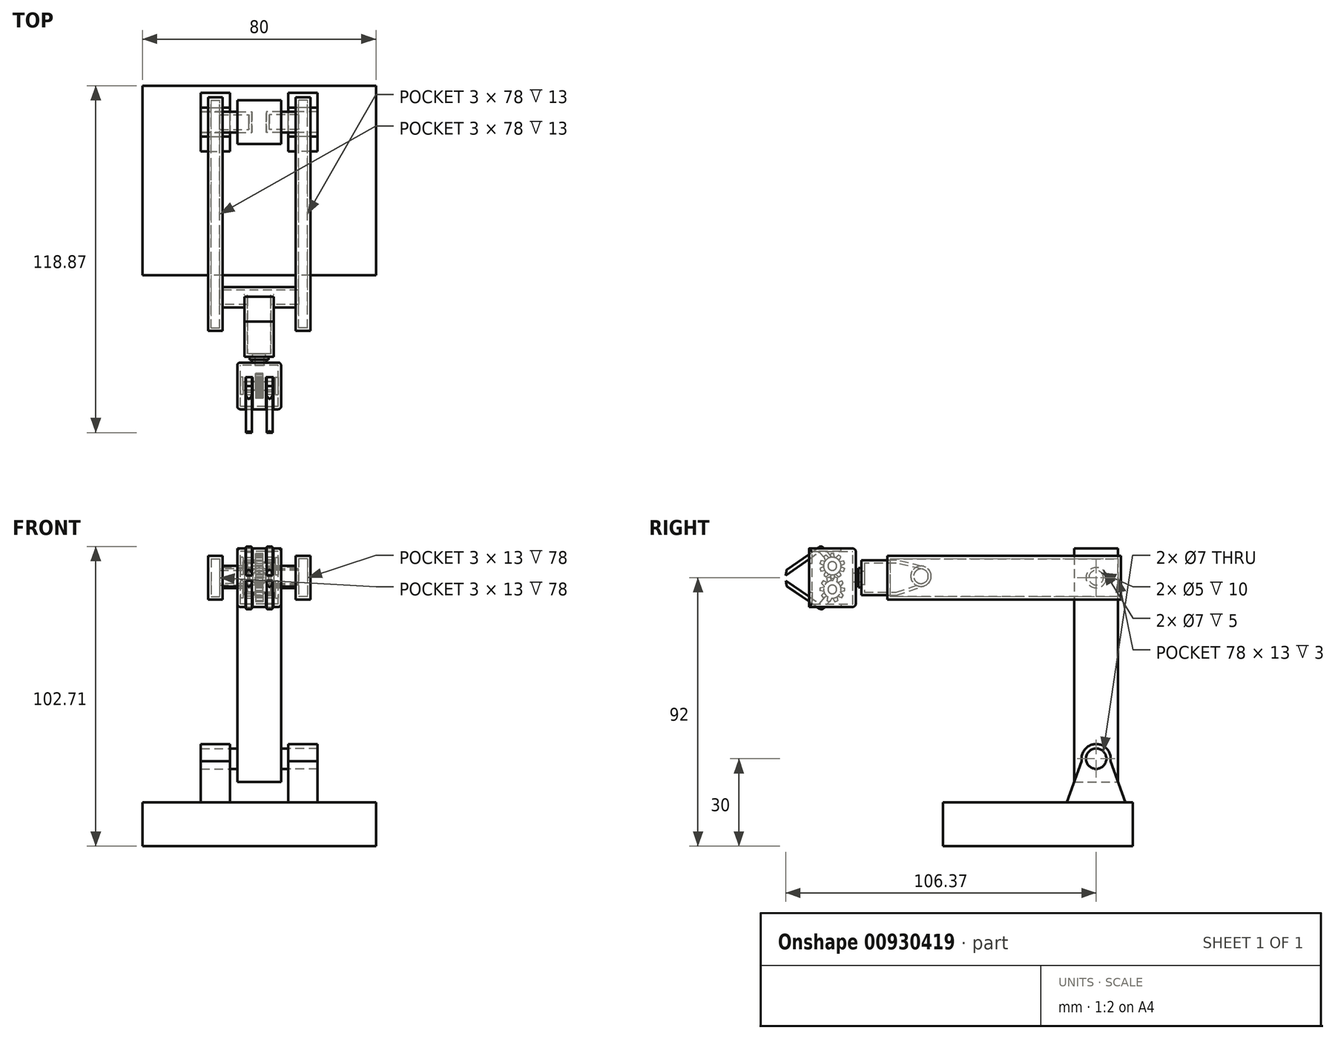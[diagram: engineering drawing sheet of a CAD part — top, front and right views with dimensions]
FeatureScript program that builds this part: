
annotation { "Feature Type Name" : "Feature", "Feature Type Description" : "" }
export const myFeature = defineFeature(function(context is Context, id is Id, definition is map)
    precondition{}
    {
        {
            var Q0;
            Q0=qCreatedBy(makeId("Top.planeOp"),FACE);
            var sketch = newSketch(context, id + "F0", { "sketchPlane" : qUnion([Q0])});
            skLineSegment(sketch, "E0.bottom", {"start": v(40, -32.5) * mm, "end": v(-40, -32.5) * mm});
            skLineSegment(sketch, "E0.top", {"start": v(40, 32.5) * mm, "end": v(-40, 32.5) * mm});
            skLineSegment(sketch, "E0.left", {"start": v(40, -32.5) * mm, "end": v(40, 32.5) * mm});
            skLineSegment(sketch, "E0.right", {"start": v(-40, -32.5) * mm, "end": v(-40, 32.5) * mm});
            skPoint(sketch, "E0.middle", {"position": v(0, 0) * mm});
            skSolve(sketch);
        }
        {
            var Q0;
            Q0 = qSketchRegion(id + "F0", true);
            extrude(context, id + "F1", {"entities" : qUnion([Q0]), "depth" : 15 * mm, "offsetDistance" : 25 * mm});
        }
        {
            var Q0;
            Q0=qCreatedBy(makeId("Right.planeOp"),FACE);
            cPlane(context, id + "F2", {"entities" : qUnion([Q0]), "cplaneType" : CPlaneType.OFFSET, "offset" : 10 * mm, "width" : 150 * mm, "height" : 150 * mm});
        }
        {
            var Q0;
            Q0=qCreatedBy(id+"F2.planeOp",FACE);
            var sketch = newSketch(context, id + "F3", { "sketchPlane" : qUnion([Q0])});
            skCircle(sketch, "E1", {"center": v(20, 30) * mm, "radius": 5 * mm});
            skLineSegment(sketch, "E2", {"start": v(15.08, 29.11) * mm, "end": v(10, 15) * mm});
            skLineSegment(sketch, "E3", {"start": v(20, 30) * mm, "end": v(20, 15) * mm, "construction": true});
            skLineSegment(sketch, "E4.MirrorCS", {"start": v(24.92, 29.11) * mm, "end": v(30, 15) * mm});
            skLineSegment(sketch, "E5", {"start": v(10, 15) * mm, "end": v(30, 15) * mm});
            skCircle(sketch, "E6", {"center": v(20, 30) * mm, "radius": 3.5 * mm});
            skSolve(sketch);
        }
        {
            var Q0;
            Q0 = qSketchRegion(id + "F3", true);
            extrude(context, id + "F4", {"entities" : qUnion([Q0]), "depth" : 10 * mm, "offsetDistance" : 25 * mm});
        }
        {
            var Q0;
            Q0=makeQuery(id+"F4.opExtrude","SWEPT_BODY",BODY,{"disambiguationData":[OSD([sQuery(id+"F3.wireOp",EDGE,"E1"),sQuery(id+"F3.wireOp",EDGE,"E2"),sQuery(id+"F3.wireOp",EDGE,"E4.MirrorCS"),sQuery(id+"F3.wireOp",EDGE,"E5"),sQuery(id+"F3.wireOp",EDGE,"E6")])]});
            var Q1;
            Q1=qCreatedBy(makeId("Right.planeOp"),FACE);
            mirror(context, id + "F5", {"operationType" : NewBodyOperationType.ADD, "entities" : qUnion([Q0]), "mirrorPlane" : qUnion([Q1])});
        }
        {
            var Q0;
            Q0=qCreatedBy(makeId("Right.planeOp"),FACE);
            var sketch = newSketch(context, id + "F6", { "sketchPlane" : qUnion([Q0])});
            skCircle(sketch, "E7.0", {"center": v(20, 30) * mm, "radius": 3.5 * mm});
            skSolve(sketch);
        }
        {
            var Q0;
            Q0 = qSketchRegion(id + "F6", true);
            extrude(context, id + "F7", {"entities" : qUnion([Q0]), "endBound" : BoundingType.SYMMETRIC, "depth" : 40 * mm, "offsetDistance" : 25 * mm});
        }
        {
            var Q0;
            Q0=qCreatedBy(makeId("Right.planeOp"),FACE);
            var sketch = newSketch(context, id + "F8", { "sketchPlane" : qUnion([Q0])});
            skLineSegment(sketch, "E8", {"start": v(12.5, 22) * mm, "end": v(27.5, 22) * mm});
            skLineSegment(sketch, "E9", {"start": v(27.5, 22) * mm, "end": v(27.5, 102) * mm});
            skLineSegment(sketch, "E10", {"start": v(27.5, 102) * mm, "end": v(12.5, 102) * mm});
            skLineSegment(sketch, "E11", {"start": v(12.5, 102) * mm, "end": v(12.5, 22) * mm});
            skSolve(sketch);
        }
        {
            var Q0;
            Q0 = qSketchRegion(id + "F8", true);
            extrude(context, id + "F9", {"entities" : qUnion([Q0]), "operationType" : NewBodyOperationType.ADD, "endBound" : BoundingType.SYMMETRIC, "depth" : 15 * mm, "offsetDistance" : 25 * mm});
        }
        {
            var Q0;
            Q0=makeQuery(id+"F9.opExtrude","CAP_FACE",FACE,{"disambiguationData":[OSD([sQuery(id+"F8.wireOp",EDGE,"E8"),sQuery(id+"F8.wireOp",EDGE,"E9"),sQuery(id+"F8.wireOp",EDGE,"E10"),sQuery(id+"F8.wireOp",EDGE,"E11")])],"isStart":false});
            var sketch = newSketch(context, id + "F10", { "sketchPlane" : qUnion([Q0])});
            skCircle(sketch, "E12", {"center": v(20, 92) * mm, "radius": 3.5 * mm});
            skSolve(sketch);
        }
        {
            var Q0;
            Q0 = qSketchRegion(id + "F10", true);
            extrude(context, id + "F11", {"entities" : qUnion([Q0]), "operationType" : NewBodyOperationType.REMOVE, "oppositeDirection" : true, "depth" : 5 * mm, "offsetDistance" : 25 * mm});
        }
        {
            var Q0;
            Q0=makeQuery(id+"F9.opExtrude","CAP_FACE",FACE,{"disambiguationData":[OSD([sQuery(id+"F8.wireOp",EDGE,"E8"),sQuery(id+"F8.wireOp",EDGE,"E9"),sQuery(id+"F8.wireOp",EDGE,"E10"),sQuery(id+"F8.wireOp",EDGE,"E11")])],"isStart":true});
            var sketch = newSketch(context, id + "F12", { "sketchPlane" : qUnion([Q0])});
            skCircle(sketch, "E13.0", {"center": v(-20, 92) * mm, "radius": 3.5 * mm});
            skSolve(sketch);
        }
        {
            var Q0;
            Q0 = qSketchRegion(id + "F12", true);
            extrude(context, id + "F13", {"entities" : qUnion([Q0]), "operationType" : NewBodyOperationType.REMOVE, "oppositeDirection" : true, "depth" : 5 * mm, "offsetDistance" : 25 * mm});
        }
        {
            var Q0;
            Q0=makeQuery(id+"F11.boolean.opBoolean","COPY",FACE,{"derivedFrom":makeQuery(id+"F11.opExtrude","CAP_FACE",FACE,{"disambiguationData":[OSD([sQuery(id+"F10.wireOp",EDGE,"E12")])],"isStart":false})});
            extrude(context, id + "F14", {"entities" : qUnion([Q0]), "depth" : 10 * mm, "offsetDistance" : 25 * mm});
        }
        {
            var Q0;
            Q0=makeQuery(id+"F14.opExtrude","CAP_FACE",FACE,{"disambiguationData":[OSD([sQuery(id+"F10.wireOp",EDGE,"E12")])],"isStart":false});
            var sketch = newSketch(context, id + "F15", { "sketchPlane" : qUnion([Q0])});
            skLineSegment(sketch, "E14", {"start": v(28.5, 99.5) * mm, "end": v(28.5, 84.5) * mm});
            skLineSegment(sketch, "E15", {"start": v(28.5, 84.5) * mm, "end": v(-51.5, 84.5) * mm});
            skLineSegment(sketch, "E16", {"start": v(-51.5, 84.5) * mm, "end": v(-51.5, 99.5) * mm});
            skLineSegment(sketch, "E17", {"start": v(-51.5, 99.5) * mm, "end": v(28.5, 99.5) * mm});
            skSolve(sketch);
        }
        {
            var Q0;
            Q0 = qSketchRegion(id + "F15", true);
            extrude(context, id + "F16", {"entities" : qUnion([Q0]), "operationType" : NewBodyOperationType.ADD, "depth" : 5 * mm, "offsetDistance" : 25 * mm});
        }
        {
            var Q0;
            Q0=makeQuery(id+"F14.opExtrude","SWEPT_BODY",BODY,{"disambiguationData":[OSD([sQuery(id+"F10.wireOp",EDGE,"E12")])]});
            var Q1;
            Q1=qCreatedBy(makeId("Right.planeOp"),FACE);
            mirror(context, id + "F17", {"entities" : qUnion([Q0]), "mirrorPlane" : qUnion([Q1])});
        }
        {
            var Q0;
            Q0=qCreatedBy(makeId("Right.planeOp"),FACE);
            var sketch = newSketch(context, id + "F18", { "sketchPlane" : qUnion([Q0])});
            skCircle(sketch, "E18", {"center": v(-40, 92.5) * mm, "radius": 3.5 * mm});
            skLineSegment(sketch, "E19", {"start": v(-38.63, 95.72) * mm, "end": v(-48.37, 98) * mm});
            skLineSegment(sketch, "E20", {"start": v(-48.37, 98) * mm, "end": v(-60.37, 98) * mm});
            skLineSegment(sketch, "E21", {"start": v(-60.37, 98) * mm, "end": v(-60.37, 86) * mm});
            skLineSegment(sketch, "E22", {"start": v(-60.37, 86) * mm, "end": v(-48.37, 86) * mm});
            skLineSegment(sketch, "E23", {"start": v(-48.37, 86) * mm, "end": v(-38.89, 89.18) * mm});
            skSolve(sketch);
        }
        {
            var Q0;
            Q0 = qSketchRegion(id + "F18", true);
            extrude(context, id + "F19", {"entities" : qUnion([Q0]), "endBound" : BoundingType.SYMMETRIC, "depth" : 10 * mm, "offsetDistance" : 25 * mm});
        }
        {
            var Q0;
            Q0=makeQuery(id+"F16.opExtrude","CAP_FACE",FACE,{"disambiguationData":[OSD([sQuery(id+"F15.wireOp",EDGE,"E14"),sQuery(id+"F15.wireOp",EDGE,"E15"),sQuery(id+"F15.wireOp",EDGE,"E16"),sQuery(id+"F15.wireOp",EDGE,"E17")])],"isStart":true});
            var sketch = newSketch(context, id + "F20", { "sketchPlane" : qUnion([Q0])});
            skCircle(sketch, "E24.0", {"center": v(40, 92.5) * mm, "radius": 3.5 * mm});
            skSolve(sketch);
        }
        {
            var Q0;
            Q0 = qSketchRegion(id + "F20", true);
            extrude(context, id + "F21", {"entities" : qUnion([Q0]), "operationType" : NewBodyOperationType.REMOVE, "oppositeDirection" : true, "depth" : 3 * mm, "offsetDistance" : 25 * mm});
        }
        {
            var Q0;
            Q0=makeQuery(id+"F17.opPattern","COPY",FACE,{"derivedFrom":makeQuery(id+"F16.opExtrude","CAP_FACE",FACE,{"disambiguationData":[OSD([sQuery(id+"F15.wireOp",EDGE,"E14"),sQuery(id+"F15.wireOp",EDGE,"E15"),sQuery(id+"F15.wireOp",EDGE,"E16"),sQuery(id+"F15.wireOp",EDGE,"E17")])],"isStart":true}),"instanceName":"1"});
            var sketch = newSketch(context, id + "F22", { "sketchPlane" : qUnion([Q0])});
            skCircle(sketch, "E25.0", {"center": v(-40, 92.5) * mm, "radius": 3.5 * mm});
            skSolve(sketch);
        }
        {
            var Q0;
            Q0 = qSketchRegion(id + "F22", true);
            extrude(context, id + "F23", {"entities" : qUnion([Q0]), "operationType" : NewBodyOperationType.REMOVE, "oppositeDirection" : true, "depth" : 3 * mm, "offsetDistance" : 25 * mm});
        }
        {
            var Q0;
            Q0=qCreatedBy(makeId("Right.planeOp"),FACE);
            var sketch = newSketch(context, id + "F24", { "sketchPlane" : qUnion([Q0])});
            skCircle(sketch, "E26.0", {"center": v(-40, 92.5) * mm, "radius": 3.5 * mm});
            skSolve(sketch);
        }
        {
            var Q0;
            Q0 = qSketchRegion(id + "F24", true);
            extrude(context, id + "F25", {"entities" : qUnion([Q0]), "operationType" : NewBodyOperationType.ADD, "endBound" : BoundingType.SYMMETRIC, "depth" : 31 * mm, "offsetDistance" : 25 * mm});
        }
        {
            var Q0;
            Q0=makeQuery(id+"F19.opExtrude","SWEPT_FACE",FACE,{"disambiguationData":[OSD([sQuery(id+"F18.wireOp",EDGE,"E21")])]});
            var sketch = newSketch(context, id + "F26", { "sketchPlane" : qUnion([Q0])});
            skCircle(sketch, "E27", {"center": v(0, 92) * mm, "radius": 2.5 * mm});
            skPoint(sketch, "E27.centerSnap0", {"position": v(5, 92) * mm});
            skCircle(sketch, "E28", {"center": v(0, 92) * mm, "radius": 3.25 * mm});
            skSolve(sketch);
        }
        {
            var Q0;
            Q0 = qSketchRegion(id + "F26", true);
            extrude(context, id + "F27", {"entities" : qUnion([Q0]), "operationType" : NewBodyOperationType.ADD, "depth" : 1 * mm, "offsetDistance" : 25 * mm});
        }
        {
            var Q0;
            Q0=makeQuery(id+"F27.boolean.opBoolean","SPLIT",FACE,{"disambiguationData":[TD([makeQuery(id+"F27.opExtrude","SWEPT_FACE",FACE,{"disambiguationData":[OSD([sQuery(id+"F26.wireOp",EDGE,"E27")])]})])],"derivedFrom":makeQuery(id+"F19.opExtrude","SWEPT_FACE",FACE,{"disambiguationData":[OSD([sQuery(id+"F18.wireOp",EDGE,"E21")])]})});
            extrude(context, id + "F28", {"entities" : qUnion([Q0]), "operationType" : NewBodyOperationType.REMOVE, "oppositeDirection" : true, "depth" : 5 * mm, "offsetDistance" : 25 * mm});
        }
        {
            var Q0;
            {var subQ0=sQuery(id+"F18.wireOp",EDGE,"E20");var subQ3=sQuery(id+"F18.wireOp",EDGE,"E21");Q0=makeQuery(id+"F27.boolean.opBoolean","SPLIT",FACE,{"disambiguationData":[TD([makeQuery(id+"F19.opExtrude","SWEPT_FACE",FACE,{"disambiguationData":[OSD([subQ0])]})])],"derivedFrom":makeQuery(id+"F19.opExtrude","SWEPT_FACE",FACE,{"disambiguationData":[OSD([subQ3])]})});}
            cPlane(context, id + "F29", {"entities" : qUnion([Q0]), "cplaneType" : CPlaneType.OFFSET, "offset" : 2 * mm, "width" : 150 * mm, "height" : 150 * mm});
        }
        {
            var Q0;
            Q0=qCreatedBy(id+"F29.planeOp",FACE);
            var sketch = newSketch(context, id + "F30", { "sketchPlane" : qUnion([Q0])});
            skLineSegment(sketch, "E29.bottom", {"start": v(7.5, 82) * mm, "end": v(-7.5, 82) * mm});
            skLineSegment(sketch, "E29.top", {"start": v(7.5, 102) * mm, "end": v(-7.5, 102) * mm});
            skLineSegment(sketch, "E29.left", {"start": v(7.5, 82) * mm, "end": v(7.5, 102) * mm});
            skLineSegment(sketch, "E29.right", {"start": v(-7.5, 82) * mm, "end": v(-7.5, 102) * mm});
            skPoint(sketch, "E29.middle", {"position": v(0, 92) * mm});
            skSolve(sketch);
        }
        {
            var Q0;
            Q0 = qSketchRegion(id + "F30", true);
            extrude(context, id + "F31", {"entities" : qUnion([Q0]), "depth" : 15 * mm, "offsetDistance" : 25 * mm});
        }
        {
            var Q0;
            Q0=makeQuery(id+"F31.opExtrude","CAP_FACE",FACE,{"disambiguationData":[OSD([sQuery(id+"F30.wireOp",EDGE,"E29.bottom"),sQuery(id+"F30.wireOp",EDGE,"E29.top"),sQuery(id+"F30.wireOp",EDGE,"E29.left"),sQuery(id+"F30.wireOp",EDGE,"E29.right")])],"isStart":true});
            var sketch = newSketch(context, id + "F32", { "sketchPlane" : qUnion([Q0])});
            skCircle(sketch, "E30.0", {"center": v(0, 92) * mm, "radius": 2.5 * mm});
            skSolve(sketch);
        }
        {
            var Q0;
            Q0 = qSketchRegion(id + "F32", true);
            extrude(context, id + "F33", {"entities" : qUnion([Q0]), "operationType" : NewBodyOperationType.ADD, "endBound" : BoundingType.UP_TO_NEXT, "depth" : 25 * mm, "offsetDistance" : 25 * mm});
        }
        {
            var Q0;
            Q0=makeQuery(id+"F31.opExtrude","CAP_FACE",FACE,{"disambiguationData":[OSD([sQuery(id+"F30.wireOp",EDGE,"E29.bottom"),sQuery(id+"F30.wireOp",EDGE,"E29.top"),sQuery(id+"F30.wireOp",EDGE,"E29.left"),sQuery(id+"F30.wireOp",EDGE,"E29.right")])],"isStart":false});
            shell(context, id + "F34", {"entities" : qUnion([Q0]), "thickness" : 1 * mm});
        }
        {
            var Q0;
            Q0=makeQuery(id+"F34.opShell","OFFSET_FACE",FACE,{"disambiguationData":[OSD([sQuery(id+"F30.wireOp",EDGE,"E29.right")])]});
            var sketch = newSketch(context, id + "F35", { "sketchPlane" : qUnion([Q0])});
            skCircle(sketch, "E31", {"center": v(-70.37, 96) * mm, "radius": 3 * mm});
            skCircle(sketch, "E32", {"center": v(-70.37, 96) * mm, "radius": 1.5 * mm});
            skSolve(sketch);
        }
        {
            var Q0;
            Q0 = qSketchRegion(id + "F35", true);
            extrude(context, id + "F36", {"entities" : qUnion([Q0]), "operationType" : NewBodyOperationType.ADD, "depth" : 1 * mm, "offsetDistance" : 25 * mm});
        }
        {
            var Q0;
            Q0=makeQuery(id+"F34.opShell","OFFSET_FACE",FACE,{"disambiguationData":[OSD([sQuery(id+"F30.wireOp",EDGE,"E29.left")])]});
            var sketch = newSketch(context, id + "F37", { "sketchPlane" : qUnion([Q0])});
            skCircle(sketch, "E33.0", {"center": v(70.37, 96) * mm, "radius": 3 * mm});
            skCircle(sketch, "E34.0", {"center": v(70.37, 96) * mm, "radius": 1.5 * mm});
            skSolve(sketch);
        }
        {
            var Q0;
            Q0 = qSketchRegion(id + "F37", true);
            extrude(context, id + "F38", {"entities" : qUnion([Q0]), "operationType" : NewBodyOperationType.ADD, "depth" : 1 * mm, "offsetDistance" : 25 * mm});
        }
        {
            var Q0;
            Q0=makeQuery(id+"F35.imprint","IMPRINT",FACE,{"disambiguationData":[TD([[makeQuery(id+"F35.imprint","IMPRINT",EDGE,{"derivedFrom":sQuery(id+"F35.wireOp",EDGE,"E31")}),-1.0]])]});
            var sketch = newSketch(context, id + "F39", { "sketchPlane" : qUnion([Q0])});
            skCircle(sketch, "E35", {"center": v(-70.37, 88) * mm, "radius": 1.5 * mm});
            skCircle(sketch, "E36", {"center": v(-70.37, 88) * mm, "radius": 3 * mm});
            skSolve(sketch);
        }
        {
            var Q0;
            Q0 = qSketchRegion(id + "F39", true);
            extrude(context, id + "F40", {"entities" : qUnion([Q0]), "operationType" : NewBodyOperationType.ADD, "depth" : 1 * mm, "offsetDistance" : 25 * mm});
        }
        {
            var Q0;
            {var subQ1=sQuery(id+"F30.wireOp",EDGE,"E29.left");var subQ3=sQuery(id+"F30.wireOp",EDGE,"E29.bottom");Q0=makeQuery(id+"F38.boolean.opBoolean","SPLIT",FACE,{"disambiguationData":[TD([makeQuery(id+"F34.opShell","OFFSET_FACE",FACE,{"disambiguationData":[OSD([subQ3])]})])],"derivedFrom":makeQuery(id+"F34.opShell","OFFSET_FACE",FACE,{"disambiguationData":[OSD([subQ1])]})});}
            var sketch = newSketch(context, id + "F41", { "sketchPlane" : qUnion([Q0])});
            skCircle(sketch, "E37.0", {"center": v(70.37, 88) * mm, "radius": 3 * mm});
            skCircle(sketch, "E38.0", {"center": v(70.37, 88) * mm, "radius": 1.5 * mm});
            skSolve(sketch);
        }
        {
            var Q0;
            Q0 = qSketchRegion(id + "F41", true);
            extrude(context, id + "F42", {"entities" : qUnion([Q0]), "operationType" : NewBodyOperationType.ADD, "depth" : 1 * mm, "offsetDistance" : 25 * mm});
        }
        {
            var Q0;
            Q0=qCreatedBy(makeId("Right.planeOp"),FACE);
            var sketch = newSketch(context, id + "F43", { "sketchPlane" : qUnion([Q0])});
            skCircle(sketch, "E39.0", {"center": v(-70.37, 96) * mm, "radius": 3 * mm});
            skLineSegment(sketch, "E40", {"start": v(-70.37, 96) * mm, "end": v(-70.37, 99) * mm, "construction": true});
            skLineSegment(sketch, "E41", {"start": v(-69.62, 98.9) * mm, "end": v(-69.87, 100.29) * mm});
            skLineSegment(sketch, "E42", {"start": v(-69.87, 100.29) * mm, "end": v(-70.37, 100.29) * mm});
            skLineSegment(sketch, "E43.MirrorCS", {"start": v(-70.87, 100.29) * mm, "end": v(-70.37, 100.29) * mm});
            skLineSegment(sketch, "E44.MirrorCS", {"start": v(-71.1, 98.9) * mm, "end": v(-70.87, 100.29) * mm});
            skLineSegment(sketch, "E45.1.0", {"start": v(-72.68, 97.91) * mm, "end": v(-73.29, 99.17) * mm});
            skLineSegment(sketch, "E45.1.1", {"start": v(-73.29, 99.17) * mm, "end": v(-72.89, 99.47) * mm});
            skLineSegment(sketch, "E45.1.2", {"start": v(-72.48, 99.76) * mm, "end": v(-72.89, 99.47) * mm});
            skLineSegment(sketch, "E45.1.3", {"start": v(-71.47, 98.79) * mm, "end": v(-72.48, 99.76) * mm});
            skLineSegment(sketch, "E45.2.0", {"start": v(-73.36, 96.2) * mm, "end": v(-74.6, 96.85) * mm});
            skLineSegment(sketch, "E45.2.1", {"start": v(-74.6, 96.85) * mm, "end": v(-74.44, 97.32) * mm});
            skLineSegment(sketch, "E45.2.2", {"start": v(-74.29, 97.8) * mm, "end": v(-74.44, 97.32) * mm});
            skLineSegment(sketch, "E45.2.3", {"start": v(-72.9, 97.6) * mm, "end": v(-74.29, 97.8) * mm});
            skLineSegment(sketch, "E46.1.3.0", {"start": v(-72.9, 94.4) * mm, "end": v(-74.29, 94.2) * mm});
            skLineSegment(sketch, "E46.3.3.0", {"start": v(-74.29, 94.2) * mm, "end": v(-74.44, 94.68) * mm});
            skLineSegment(sketch, "E46.6.3.0", {"start": v(-74.6, 95.15) * mm, "end": v(-74.44, 94.68) * mm});
            skLineSegment(sketch, "E46.9.3.0", {"start": v(-73.36, 95.8) * mm, "end": v(-74.6, 95.15) * mm});
            skLineSegment(sketch, "E46.1.4.0", {"start": v(-71.47, 93.21) * mm, "end": v(-72.48, 92.24) * mm});
            skLineSegment(sketch, "E46.3.4.0", {"start": v(-72.48, 92.24) * mm, "end": v(-72.89, 92.53) * mm});
            skLineSegment(sketch, "E46.6.4.0", {"start": v(-73.29, 92.83) * mm, "end": v(-72.89, 92.53) * mm});
            skLineSegment(sketch, "E46.9.4.0", {"start": v(-72.68, 94.09) * mm, "end": v(-73.29, 92.83) * mm});
            skLineSegment(sketch, "E46.1.5.0", {"start": v(-69.62, 93.1) * mm, "end": v(-69.87, 91.71) * mm});
            skLineSegment(sketch, "E46.3.5.0", {"start": v(-69.87, 91.71) * mm, "end": v(-70.37, 91.71) * mm});
            skLineSegment(sketch, "E46.6.5.0", {"start": v(-70.87, 91.71) * mm, "end": v(-70.37, 91.71) * mm});
            skLineSegment(sketch, "E46.9.5.0", {"start": v(-71.1, 93.1) * mm, "end": v(-70.87, 91.71) * mm});
            skLineSegment(sketch, "E46.1.6.0", {"start": v(-68.06, 94.09) * mm, "end": v(-67.44, 92.83) * mm});
            skLineSegment(sketch, "E46.3.6.0", {"start": v(-67.44, 92.83) * mm, "end": v(-67.85, 92.53) * mm});
            skLineSegment(sketch, "E46.6.6.0", {"start": v(-68.25, 92.24) * mm, "end": v(-67.85, 92.53) * mm});
            skLineSegment(sketch, "E46.9.6.0", {"start": v(-69.26, 93.21) * mm, "end": v(-68.25, 92.24) * mm});
            skLineSegment(sketch, "E46.1.7.0", {"start": v(-67.37, 95.8) * mm, "end": v(-66.14, 95.15) * mm});
            skLineSegment(sketch, "E46.3.7.0", {"start": v(-66.14, 95.15) * mm, "end": v(-66.3, 94.68) * mm});
            skLineSegment(sketch, "E46.6.7.0", {"start": v(-66.45, 94.2) * mm, "end": v(-66.3, 94.68) * mm});
            skLineSegment(sketch, "E46.9.7.0", {"start": v(-67.83, 94.4) * mm, "end": v(-66.45, 94.2) * mm});
            skLineSegment(sketch, "E46.1.8.0", {"start": v(-67.83, 97.6) * mm, "end": v(-66.45, 97.8) * mm});
            skLineSegment(sketch, "E46.3.8.0", {"start": v(-66.45, 97.8) * mm, "end": v(-66.3, 97.32) * mm});
            skLineSegment(sketch, "E46.6.8.0", {"start": v(-66.14, 96.85) * mm, "end": v(-66.3, 97.32) * mm});
            skLineSegment(sketch, "E46.9.8.0", {"start": v(-67.37, 96.2) * mm, "end": v(-66.14, 96.85) * mm});
            skLineSegment(sketch, "E46.1.9.0", {"start": v(-69.26, 98.79) * mm, "end": v(-68.25, 99.76) * mm});
            skLineSegment(sketch, "E46.3.9.0", {"start": v(-68.25, 99.76) * mm, "end": v(-67.85, 99.47) * mm});
            skLineSegment(sketch, "E46.6.9.0", {"start": v(-67.44, 99.17) * mm, "end": v(-67.85, 99.47) * mm});
            skLineSegment(sketch, "E46.9.9.0", {"start": v(-68.06, 97.91) * mm, "end": v(-67.44, 99.17) * mm});
            skSolve(sketch);
        }
        {
            var Q0;
            Q0 = qSketchRegion(id + "F43", true);
            extrude(context, id + "F44", {"entities" : qUnion([Q0]), "endBound" : BoundingType.SYMMETRIC, "depth" : 2.5 * mm, "offsetDistance" : 25 * mm});
        }
        {
            var Q0;
            Q0=makeQuery(id+"F38.boolean.opBoolean","SPLIT",FACE,{"disambiguationData":[TD([makeQuery(id+"F38.opExtrude","SWEPT_FACE",FACE,{"disambiguationData":[OSD([sQuery(id+"F37.wireOp",EDGE,"E34.0")])]})])],"derivedFrom":makeQuery(id+"F34.opShell","OFFSET_FACE",FACE,{"disambiguationData":[OSD([sQuery(id+"F30.wireOp",EDGE,"E29.left")])]})});
            extrude(context, id + "F45", {"entities" : qUnion([Q0]), "operationType" : NewBodyOperationType.ADD, "depth" : 13 * mm, "offsetDistance" : 25 * mm});
        }
        {
            var Q0;
            Q0=qCreatedBy(makeId("Right.planeOp"),FACE);
            var sketch = newSketch(context, id + "F46", { "sketchPlane" : qUnion([Q0])});
            skCircle(sketch, "E47.0", {"center": v(-70.37, 88) * mm, "radius": 3 * mm});
            skLineSegment(sketch, "E48", {"start": v(-70.37, 88) * mm, "end": v(-67.37, 88) * mm, "construction": true});
            skLineSegment(sketch, "E49", {"start": v(-67.46, 87.26) * mm, "end": v(-66.08, 87.5) * mm});
            skLineSegment(sketch, "E50", {"start": v(-66.08, 87.5) * mm, "end": v(-66.08, 88) * mm});
            skLineSegment(sketch, "E51.MirrorCS", {"start": v(-67.46, 88.74) * mm, "end": v(-66.08, 88.5) * mm});
            skLineSegment(sketch, "E52.MirrorCS", {"start": v(-66.08, 88.5) * mm, "end": v(-66.08, 88) * mm});
            skLineSegment(sketch, "E53.1.0", {"start": v(-68.45, 90.3) * mm, "end": v(-67.2, 90.92) * mm});
            skLineSegment(sketch, "E53.1.1", {"start": v(-67.2, 90.92) * mm, "end": v(-66.9, 90.52) * mm});
            skLineSegment(sketch, "E53.1.2", {"start": v(-66.6, 90.11) * mm, "end": v(-66.9, 90.52) * mm});
            skLineSegment(sketch, "E53.1.3", {"start": v(-67.58, 89.1) * mm, "end": v(-66.6, 90.11) * mm});
            skLineSegment(sketch, "E53.2.0", {"start": v(-70.18, 91) * mm, "end": v(-69.52, 92.23) * mm});
            skLineSegment(sketch, "E53.2.1", {"start": v(-69.52, 92.23) * mm, "end": v(-69.04, 92.08) * mm});
            skLineSegment(sketch, "E53.2.2", {"start": v(-68.57, 91.92) * mm, "end": v(-69.04, 92.08) * mm});
            skLineSegment(sketch, "E53.2.3", {"start": v(-68.76, 90.53) * mm, "end": v(-68.57, 91.92) * mm});
            skLineSegment(sketch, "E54.1.3.0", {"start": v(-71.97, 90.53) * mm, "end": v(-72.17, 91.92) * mm});
            skLineSegment(sketch, "E54.3.3.0", {"start": v(-72.17, 91.92) * mm, "end": v(-71.7, 92.08) * mm});
            skLineSegment(sketch, "E54.6.3.0", {"start": v(-71.22, 92.23) * mm, "end": v(-71.7, 92.08) * mm});
            skLineSegment(sketch, "E54.9.3.0", {"start": v(-70.56, 91) * mm, "end": v(-71.22, 92.23) * mm});
            skLineSegment(sketch, "E54.1.4.0", {"start": v(-73.15, 89.1) * mm, "end": v(-74.13, 90.11) * mm});
            skLineSegment(sketch, "E54.3.4.0", {"start": v(-74.13, 90.11) * mm, "end": v(-73.83, 90.52) * mm});
            skLineSegment(sketch, "E54.6.4.0", {"start": v(-73.54, 90.92) * mm, "end": v(-73.83, 90.52) * mm});
            skLineSegment(sketch, "E54.9.4.0", {"start": v(-72.28, 90.3) * mm, "end": v(-73.54, 90.92) * mm});
            skLineSegment(sketch, "E54.1.5.0", {"start": v(-73.27, 87.26) * mm, "end": v(-74.65, 87.5) * mm});
            skLineSegment(sketch, "E54.3.5.0", {"start": v(-74.65, 87.5) * mm, "end": v(-74.65, 88) * mm});
            skLineSegment(sketch, "E54.6.5.0", {"start": v(-74.65, 88.5) * mm, "end": v(-74.65, 88) * mm});
            skLineSegment(sketch, "E54.9.5.0", {"start": v(-73.27, 88.74) * mm, "end": v(-74.65, 88.5) * mm});
            skLineSegment(sketch, "E54.1.6.0", {"start": v(-72.28, 85.7) * mm, "end": v(-73.54, 85.08) * mm});
            skLineSegment(sketch, "E54.3.6.0", {"start": v(-73.54, 85.08) * mm, "end": v(-73.83, 85.48) * mm});
            skLineSegment(sketch, "E54.6.6.0", {"start": v(-74.13, 85.89) * mm, "end": v(-73.83, 85.48) * mm});
            skLineSegment(sketch, "E54.9.6.0", {"start": v(-73.15, 86.9) * mm, "end": v(-74.13, 85.89) * mm});
            skLineSegment(sketch, "E54.1.7.0", {"start": v(-70.56, 85) * mm, "end": v(-71.22, 83.77) * mm});
            skLineSegment(sketch, "E54.3.7.0", {"start": v(-71.22, 83.77) * mm, "end": v(-71.7, 83.92) * mm});
            skLineSegment(sketch, "E54.6.7.0", {"start": v(-72.17, 84.08) * mm, "end": v(-71.7, 83.92) * mm});
            skLineSegment(sketch, "E54.9.7.0", {"start": v(-71.97, 85.47) * mm, "end": v(-72.17, 84.08) * mm});
            skLineSegment(sketch, "E54.1.8.0", {"start": v(-68.76, 85.47) * mm, "end": v(-68.57, 84.08) * mm});
            skLineSegment(sketch, "E54.3.8.0", {"start": v(-68.57, 84.08) * mm, "end": v(-69.04, 83.92) * mm});
            skLineSegment(sketch, "E54.6.8.0", {"start": v(-69.52, 83.77) * mm, "end": v(-69.04, 83.92) * mm});
            skLineSegment(sketch, "E54.9.8.0", {"start": v(-70.18, 85) * mm, "end": v(-69.52, 83.77) * mm});
            skLineSegment(sketch, "E54.1.9.0", {"start": v(-67.58, 86.9) * mm, "end": v(-66.6, 85.89) * mm});
            skLineSegment(sketch, "E54.3.9.0", {"start": v(-66.6, 85.89) * mm, "end": v(-66.9, 85.48) * mm});
            skLineSegment(sketch, "E54.6.9.0", {"start": v(-67.2, 85.08) * mm, "end": v(-66.9, 85.48) * mm});
            skLineSegment(sketch, "E54.9.9.0", {"start": v(-68.45, 85.7) * mm, "end": v(-67.2, 85.08) * mm});
            skSolve(sketch);
        }
        {
            var Q0;
            Q0 = qSketchRegion(id + "F46", true);
            extrude(context, id + "F47", {"entities" : qUnion([Q0]), "endBound" : BoundingType.SYMMETRIC, "depth" : 2.5 * mm, "offsetDistance" : 25 * mm});
        }
        {
            var Q0;
            Q0=makeQuery(id+"F39.imprint","IMPRINT",FACE,{"disambiguationData":[TD([[makeQuery(id+"F39.imprint","IMPRINT",EDGE,{"derivedFrom":sQuery(id+"F39.wireOp",EDGE,"E35")}),1.0]])]});
            extrude(context, id + "F48", {"entities" : qUnion([Q0]), "operationType" : NewBodyOperationType.ADD, "depth" : 13 * mm, "offsetDistance" : 25 * mm});
        }
        {
            var Q0;
            Q0=makeQuery(id+"F31.opExtrude","SWEPT_FACE",FACE,{"disambiguationData":[OSD([sQuery(id+"F30.wireOp",EDGE,"E29.top")])]});
            var sketch = newSketch(context, id + "F49", { "sketchPlane" : qUnion([Q0])});
            skLineSegment(sketch, "E55", {"start": v(2.3, -77.37) * mm, "end": v(2.3, -67.37) * mm});
            skLineSegment(sketch, "E56", {"start": v(2.3, -67.37) * mm, "end": v(4.8, -67.37) * mm});
            skLineSegment(sketch, "E57", {"start": v(4.8, -67.37) * mm, "end": v(4.8, -77.37) * mm});
            skLineSegment(sketch, "E58.1.0.0", {"start": v(-4.7, -77.37) * mm, "end": v(-4.7, -67.37) * mm});
            skLineSegment(sketch, "E58.1.0.1", {"start": v(-4.7, -67.37) * mm, "end": v(-2.2, -67.37) * mm});
            skLineSegment(sketch, "E58.1.0.2", {"start": v(-2.2, -67.37) * mm, "end": v(-2.2, -77.37) * mm});
            skLineSegment(sketch, "E58.direction1", {"start": v(2.3, -77.37) * mm, "end": v(-4.7, -77.37) * mm, "construction": true});
            skSolve(sketch);
        }
        {
            var Q0;
            {var subQ0=sQuery(id+"F49.wireOp",EDGE,"E58.1.0.0");Q0=makeQuery(id+"F49.imprint","IMPRINT",FACE,{"disambiguationData":[TD([[makeQuery(id+"F49.imprint","IMPRINT",EDGE,{"derivedFrom":subQ0}),-1.0]])]});}
            extrude(context, id + "F50", {"entities" : qUnion([Q0]), "operationType" : NewBodyOperationType.REMOVE, "oppositeDirection" : true, "depth" : 2 * mm, "offsetDistance" : 25 * mm});
        }
        {
            var Q0;
            {var subQ0=sQuery(id+"F49.wireOp",EDGE,"E55");Q0=makeQuery(id+"F49.imprint","IMPRINT",FACE,{"disambiguationData":[TD([[makeQuery(id+"F49.imprint","IMPRINT",EDGE,{"derivedFrom":subQ0}),-1.0]])]});}
            extrude(context, id + "F51", {"entities" : qUnion([Q0]), "operationType" : NewBodyOperationType.REMOVE, "oppositeDirection" : true, "depth" : 2 * mm, "offsetDistance" : 25 * mm});
        }
        {
            var Q0;
            Q0=makeQuery(id+"F44.opExtrude","CAP_FACE",FACE,{"disambiguationData":[OSD([sQuery(id+"F43.wireOp",EDGE,"E39.0"),sQuery(id+"F43.wireOp",EDGE,"E41"),sQuery(id+"F43.wireOp",EDGE,"E42"),sQuery(id+"F43.wireOp",EDGE,"E43.MirrorCS"),sQuery(id+"F43.wireOp",EDGE,"E44.MirrorCS"),sQuery(id+"F43.wireOp",EDGE,"E45.1.0"),sQuery(id+"F43.wireOp",EDGE,"E45.1.1"),sQuery(id+"F43.wireOp",EDGE,"E45.1.2"),sQuery(id+"F43.wireOp",EDGE,"E45.1.3"),sQuery(id+"F43.wireOp",EDGE,"E45.2.0"),sQuery(id+"F43.wireOp",EDGE,"E45.2.1"),sQuery(id+"F43.wireOp",EDGE,"E45.2.2"),sQuery(id+"F43.wireOp",EDGE,"E45.2.3"),sQuery(id+"F43.wireOp",EDGE,"E46.1.3.0"),sQuery(id+"F43.wireOp",EDGE,"E46.3.3.0"),sQuery(id+"F43.wireOp",EDGE,"E46.6.3.0"),sQuery(id+"F43.wireOp",EDGE,"E46.9.3.0"),sQuery(id+"F43.wireOp",EDGE,"E46.1.4.0"),sQuery(id+"F43.wireOp",EDGE,"E46.3.4.0"),sQuery(id+"F43.wireOp",EDGE,"E46.6.4.0"),sQuery(id+"F43.wireOp",EDGE,"E46.9.4.0"),sQuery(id+"F43.wireOp",EDGE,"E46.1.5.0"),sQuery(id+"F43.wireOp",EDGE,"E46.3.5.0"),sQuery(id+"F43.wireOp",EDGE,"E46.6.5.0"),sQuery(id+"F43.wireOp",EDGE,"E46.9.5.0"),sQuery(id+"F43.wireOp",EDGE,"E46.1.6.0"),sQuery(id+"F43.wireOp",EDGE,"E46.3.6.0"),sQuery(id+"F43.wireOp",EDGE,"E46.6.6.0"),sQuery(id+"F43.wireOp",EDGE,"E46.9.6.0"),sQuery(id+"F43.wireOp",EDGE,"E46.1.7.0"),sQuery(id+"F43.wireOp",EDGE,"E46.3.7.0"),sQuery(id+"F43.wireOp",EDGE,"E46.6.7.0"),sQuery(id+"F43.wireOp",EDGE,"E46.9.7.0"),sQuery(id+"F43.wireOp",EDGE,"E46.1.8.0"),sQuery(id+"F43.wireOp",EDGE,"E46.3.8.0"),sQuery(id+"F43.wireOp",EDGE,"E46.6.8.0"),sQuery(id+"F43.wireOp",EDGE,"E46.9.8.0"),sQuery(id+"F43.wireOp",EDGE,"E46.1.9.0"),sQuery(id+"F43.wireOp",EDGE,"E46.3.9.0"),sQuery(id+"F43.wireOp",EDGE,"E46.6.9.0"),sQuery(id+"F43.wireOp",EDGE,"E46.9.9.0")])],"isStart":false});
            cPlane(context, id + "F52", {"entities" : qUnion([Q0]), "cplaneType" : CPlaneType.OFFSET, "offset" : 2.3 * mm, "width" : 150 * mm, "height" : 150 * mm});
        }
        {
            var Q0;
            Q0=qCreatedBy(id+"F52.planeOp",FACE);
            var sketch = newSketch(context, id + "F53", { "sketchPlane" : qUnion([Q0])});
            skCircle(sketch, "E59.0", {"center": v(-70.37, 96) * mm, "radius": 3 * mm});
            skCircle(sketch, "E60.0", {"center": v(-70.37, 96) * mm, "radius": 1.5 * mm});
            skLineSegment(sketch, "E61", {"start": v(-70.41, 99) * mm, "end": v(-74.16, 103.03) * mm});
            skLineSegment(sketch, "E62", {"start": v(-74.16, 103.03) * mm, "end": v(-86, 94.67) * mm});
            skLineSegment(sketch, "E63", {"start": v(-86.37, 92.7) * mm, "end": v(-74.92, 100.77) * mm});
            skLineSegment(sketch, "E64", {"start": v(-74.92, 100.77) * mm, "end": v(-72.47, 98.14) * mm});
            skLineSegment(sketch, "E65", {"start": v(-86, 94.67) * mm, "end": v(-86.37, 92.7) * mm});
            skSolve(sketch);
        }
        {
            var Q0;
            Q0 = qSketchRegion(id + "F53", true);
            extrude(context, id + "F54", {"entities" : qUnion([Q0]), "endBound" : BoundingType.SYMMETRIC, "depth" : 2 * mm, "offsetDistance" : 25 * mm});
        }
        {
            var Q0;
            Q0=makeQuery(id+"F54.opExtrude","SWEPT_BODY",BODY,{"disambiguationData":[OSD([sQuery(id+"F53.wireOp",EDGE,"E59.0"),sQuery(id+"F53.wireOp",EDGE,"E60.0"),sQuery(id+"F53.wireOp",EDGE,"E61"),sQuery(id+"F53.wireOp",EDGE,"E62"),sQuery(id+"F53.wireOp",EDGE,"E63"),sQuery(id+"F53.wireOp",EDGE,"E64"),sQuery(id+"F53.wireOp",EDGE,"E65")])]});
            var Q1;
            Q1=qCreatedBy(makeId("Right.planeOp"),FACE);
            mirror(context, id + "F55", {"entities" : qUnion([Q0]), "mirrorPlane" : qUnion([Q1])});
        }
        {
            var Q0;
            Q0=makeQuery(id+"F31.opExtrude","SWEPT_FACE",FACE,{"disambiguationData":[OSD([sQuery(id+"F30.wireOp",EDGE,"E29.bottom")])]});
            var sketch = newSketch(context, id + "F56", { "sketchPlane" : qUnion([Q0])});
            skLineSegment(sketch, "E66.0", {"start": v(-4.7, 77.37) * mm, "end": v(-4.7, 67.37) * mm});
            skLineSegment(sketch, "E67.0", {"start": v(-2.2, 67.37) * mm, "end": v(-2.2, 77.37) * mm});
            skLineSegment(sketch, "E68.0", {"start": v(-4.7, 67.37) * mm, "end": v(-2.2, 67.37) * mm});
            skLineSegment(sketch, "E69.0", {"start": v(2.3, 77.37) * mm, "end": v(2.3, 67.37) * mm});
            skLineSegment(sketch, "E70.0", {"start": v(2.3, 67.37) * mm, "end": v(4.8, 67.37) * mm});
            skLineSegment(sketch, "E71.0", {"start": v(4.8, 67.37) * mm, "end": v(4.8, 77.37) * mm});
            skSolve(sketch);
        }
        {
            var Q0;
            {var subQ0=sQuery(id+"F56.wireOp",EDGE,"E66.0");Q0=makeQuery(id+"F56.imprint","IMPRINT",FACE,{"disambiguationData":[TD([[makeQuery(id+"F56.imprint","IMPRINT",EDGE,{"derivedFrom":subQ0}),1.0]])]});}
            extrude(context, id + "F57", {"entities" : qUnion([Q0]), "operationType" : NewBodyOperationType.REMOVE, "oppositeDirection" : true, "depth" : 2 * mm, "offsetDistance" : 25 * mm});
        }
        {
            var Q0;
            {var subQ0=sQuery(id+"F56.wireOp",EDGE,"E69.0");Q0=makeQuery(id+"F56.imprint","IMPRINT",FACE,{"disambiguationData":[TD([[makeQuery(id+"F56.imprint","IMPRINT",EDGE,{"derivedFrom":subQ0}),1.0]])]});}
            extrude(context, id + "F58", {"entities" : qUnion([Q0]), "operationType" : NewBodyOperationType.REMOVE, "oppositeDirection" : true, "depth" : 2 * mm, "offsetDistance" : 25 * mm});
        }
        {
            var Q0;
            Q0=makeQuery(id+"F47.opExtrude","CAP_FACE",FACE,{"disambiguationData":[OSD([sQuery(id+"F46.wireOp",EDGE,"E47.0"),sQuery(id+"F46.wireOp",EDGE,"E49"),sQuery(id+"F46.wireOp",EDGE,"E50"),sQuery(id+"F46.wireOp",EDGE,"E51.MirrorCS"),sQuery(id+"F46.wireOp",EDGE,"E52.MirrorCS"),sQuery(id+"F46.wireOp",EDGE,"E53.1.0"),sQuery(id+"F46.wireOp",EDGE,"E53.1.1"),sQuery(id+"F46.wireOp",EDGE,"E53.1.2"),sQuery(id+"F46.wireOp",EDGE,"E53.1.3"),sQuery(id+"F46.wireOp",EDGE,"E53.2.0"),sQuery(id+"F46.wireOp",EDGE,"E53.2.1"),sQuery(id+"F46.wireOp",EDGE,"E53.2.2"),sQuery(id+"F46.wireOp",EDGE,"E53.2.3"),sQuery(id+"F46.wireOp",EDGE,"E54.1.3.0"),sQuery(id+"F46.wireOp",EDGE,"E54.3.3.0"),sQuery(id+"F46.wireOp",EDGE,"E54.6.3.0"),sQuery(id+"F46.wireOp",EDGE,"E54.9.3.0"),sQuery(id+"F46.wireOp",EDGE,"E54.1.4.0"),sQuery(id+"F46.wireOp",EDGE,"E54.3.4.0"),sQuery(id+"F46.wireOp",EDGE,"E54.6.4.0"),sQuery(id+"F46.wireOp",EDGE,"E54.9.4.0"),sQuery(id+"F46.wireOp",EDGE,"E54.1.5.0"),sQuery(id+"F46.wireOp",EDGE,"E54.3.5.0"),sQuery(id+"F46.wireOp",EDGE,"E54.6.5.0"),sQuery(id+"F46.wireOp",EDGE,"E54.9.5.0"),sQuery(id+"F46.wireOp",EDGE,"E54.1.6.0"),sQuery(id+"F46.wireOp",EDGE,"E54.3.6.0"),sQuery(id+"F46.wireOp",EDGE,"E54.6.6.0"),sQuery(id+"F46.wireOp",EDGE,"E54.9.6.0"),sQuery(id+"F46.wireOp",EDGE,"E54.1.7.0"),sQuery(id+"F46.wireOp",EDGE,"E54.3.7.0"),sQuery(id+"F46.wireOp",EDGE,"E54.6.7.0"),sQuery(id+"F46.wireOp",EDGE,"E54.9.7.0"),sQuery(id+"F46.wireOp",EDGE,"E54.1.8.0"),sQuery(id+"F46.wireOp",EDGE,"E54.3.8.0"),sQuery(id+"F46.wireOp",EDGE,"E54.6.8.0"),sQuery(id+"F46.wireOp",EDGE,"E54.9.8.0"),sQuery(id+"F46.wireOp",EDGE,"E54.1.9.0"),sQuery(id+"F46.wireOp",EDGE,"E54.3.9.0"),sQuery(id+"F46.wireOp",EDGE,"E54.6.9.0"),sQuery(id+"F46.wireOp",EDGE,"E54.9.9.0")])],"isStart":false});
            cPlane(context, id + "F59", {"entities" : qUnion([Q0]), "cplaneType" : CPlaneType.OFFSET, "offset" : 2.3 * mm, "width" : 150 * mm, "height" : 150 * mm});
        }
        {
            var Q0;
            Q0=qCreatedBy(id+"F59.planeOp",FACE);
            var sketch = newSketch(context, id + "F60", { "sketchPlane" : qUnion([Q0])});
            skCircle(sketch, "E72.0", {"center": v(-70.37, 88) * mm, "radius": 3 * mm});
            skCircle(sketch, "E73.0", {"center": v(-70.37, 88) * mm, "radius": 1.5 * mm});
            skLineSegment(sketch, "E74", {"start": v(-70.37, 85) * mm, "end": v(-73.95, 80.83) * mm});
            skLineSegment(sketch, "E75", {"start": v(-73.95, 80.83) * mm, "end": v(-85.94, 88.99) * mm});
            skLineSegment(sketch, "E76", {"start": v(-85.94, 88.99) * mm, "end": v(-86.37, 90.94) * mm});
            skLineSegment(sketch, "E77", {"start": v(-86.37, 90.94) * mm, "end": v(-74.78, 83.1) * mm});
            skLineSegment(sketch, "E78", {"start": v(-74.78, 83.1) * mm, "end": v(-72.43, 85.82) * mm});
            skSolve(sketch);
        }
        {
            var Q0;
            Q0 = qSketchRegion(id + "F60", true);
            extrude(context, id + "F61", {"entities" : qUnion([Q0]), "endBound" : BoundingType.SYMMETRIC, "depth" : 2 * mm, "offsetDistance" : 25 * mm});
        }
        {
            var Q0;
            Q0=makeQuery(id+"F61.opExtrude","SWEPT_BODY",BODY,{"disambiguationData":[OSD([sQuery(id+"F60.wireOp",EDGE,"E72.0"),sQuery(id+"F60.wireOp",EDGE,"E73.0"),sQuery(id+"F60.wireOp",EDGE,"E74"),sQuery(id+"F60.wireOp",EDGE,"E75"),sQuery(id+"F60.wireOp",EDGE,"E76"),sQuery(id+"F60.wireOp",EDGE,"E77"),sQuery(id+"F60.wireOp",EDGE,"E78")])]});
            var Q1;
            Q1=qCreatedBy(makeId("Right.planeOp"),FACE);
            mirror(context, id + "F62", {"entities" : qUnion([Q0]), "mirrorPlane" : qUnion([Q1])});
        }
        {
            var Q0;
            {var subQ0=sQuery(id+"F30.wireOp",EDGE,"E29.top");var subQ2=sQuery(id+"F30.wireOp",EDGE,"E29.bottom");var subQ4=sQuery(id+"F30.wireOp",EDGE,"E29.right");var subQ5=makeQuery(id+"F31.opExtrude","SWEPT_FACE",FACE,{"disambiguationData":[OSD([subQ4])]});var subQ6=makeQuery(id+"F31.opExtrude","SWEPT_FACE",FACE,{"disambiguationData":[OSD([subQ2])]});var subQ10=sQuery(id+"F30.wireOp",EDGE,"E29.left");Q0=makeQuery(id+"F57.boolean.opBoolean","SPLIT",FACE,{"disambiguationData":[TD([subQ5])],"derivedFrom":makeQuery(id+"F51.boolean.opBoolean","SPLIT",FACE,{"disambiguationData":[TD([subQ6])],"derivedFrom":makeQuery(id+"F31.opExtrude","CAP_FACE",FACE,{"disambiguationData":[OSD([subQ2,subQ0,subQ10,subQ4])],"isStart":false})})});}
            var sketch = newSketch(context, id + "F63", { "sketchPlane" : qUnion([Q0])});
            skLineSegment(sketch, "E79.bottom", {"start": v(-7.5, 102) * mm, "end": v(-4.7, 102) * mm});
            skLineSegment(sketch, "E79.top", {"start": v(-7.5, 82) * mm, "end": v(-4.7, 82) * mm});
            skLineSegment(sketch, "E79.left", {"start": v(-7.5, 102) * mm, "end": v(-7.5, 82) * mm});
            skLineSegment(sketch, "E79.right", {"start": v(7.5, 102) * mm, "end": v(7.5, 82) * mm});
            skLineSegment(sketch, "E80", {"start": v(-4.7, 82) * mm, "end": v(-4.7, 87) * mm});
            skLineSegment(sketch, "E81", {"start": v(-2.2, 82) * mm, "end": v(-2.2, 87) * mm});
            skLineSegment(sketch, "E82", {"start": v(-2.2, 87) * mm, "end": v(-4.7, 87) * mm});
            skLineSegment(sketch, "E83", {"start": v(2.3, 82) * mm, "end": v(2.3, 87) * mm});
            skLineSegment(sketch, "E84", {"start": v(2.3, 87) * mm, "end": v(4.8, 87) * mm});
            skLineSegment(sketch, "E85", {"start": v(4.8, 87) * mm, "end": v(4.8, 82) * mm});
            skLineSegment(sketch, "E86", {"start": v(-4.7, 102) * mm, "end": v(-4.7, 97) * mm});
            skLineSegment(sketch, "E87", {"start": v(-4.7, 97) * mm, "end": v(-2.2, 97) * mm});
            skLineSegment(sketch, "E88", {"start": v(-2.2, 97) * mm, "end": v(-2.2, 102) * mm});
            skLineSegment(sketch, "E89", {"start": v(2.3, 102) * mm, "end": v(2.3, 97) * mm});
            skLineSegment(sketch, "E90", {"start": v(2.3, 97) * mm, "end": v(4.8, 97) * mm});
            skLineSegment(sketch, "E91", {"start": v(4.8, 97) * mm, "end": v(4.8, 102) * mm});
            skLineSegment(sketch, "E92.trimOffspring", {"start": v(-2.2, 102) * mm, "end": v(2.3, 102) * mm});
            skLineSegment(sketch, "E93.trimOffspring", {"start": v(4.8, 102) * mm, "end": v(7.5, 102) * mm});
            skLineSegment(sketch, "E94.trimOffspring", {"start": v(-2.2, 82) * mm, "end": v(2.3, 82) * mm});
            skLineSegment(sketch, "E95.trimOffspring", {"start": v(4.8, 82) * mm, "end": v(7.5, 82) * mm});
            skSolve(sketch);
        }
        {
            var Q0;
            Q0 = qSketchRegion(id + "F63", true);
            extrude(context, id + "F64", {"entities" : qUnion([Q0]), "operationType" : NewBodyOperationType.ADD, "depth" : 1 * mm, "offsetDistance" : 25 * mm});
        }
        {
            var Q0;
            Q0=makeQuery(id+"F64.boolean.opBoolean","MERGE",EDGE,{"derivedFrom":[makeQuery(id+"F31.opExtrude","SWEPT_EDGE",EDGE,{"disambiguationData":[OSD([sQuery(id+"F30.wireOp",EDGE,"E29.top"),sQuery(id+"F30.wireOp",EDGE,"E29.left")])]}),makeQuery(id+"F64.opExtrude","SWEPT_EDGE",EDGE,{"disambiguationData":[OSD([sQuery(id+"F63.wireOp",EDGE,"E79.right"),sQuery(id+"F63.wireOp",EDGE,"E93.trimOffspring")])]})]});
            var Q1;
            Q1=makeQuery(id+"F64.boolean.opBoolean","MERGE",EDGE,{"derivedFrom":[makeQuery(id+"F31.opExtrude","SWEPT_EDGE",EDGE,{"disambiguationData":[OSD([sQuery(id+"F30.wireOp",EDGE,"E29.bottom"),sQuery(id+"F30.wireOp",EDGE,"E29.left")])]}),makeQuery(id+"F64.opExtrude","SWEPT_EDGE",EDGE,{"disambiguationData":[OSD([sQuery(id+"F63.wireOp",EDGE,"E79.right"),sQuery(id+"F63.wireOp",EDGE,"E95.trimOffspring")])]})]});
            var Q2;
            Q2=makeQuery(id+"F64.boolean.opBoolean","MERGE",EDGE,{"derivedFrom":[makeQuery(id+"F31.opExtrude","SWEPT_EDGE",EDGE,{"disambiguationData":[OSD([sQuery(id+"F30.wireOp",EDGE,"E29.top"),sQuery(id+"F30.wireOp",EDGE,"E29.right")])]}),makeQuery(id+"F64.opExtrude","SWEPT_EDGE",EDGE,{"disambiguationData":[OSD([sQuery(id+"F63.wireOp",EDGE,"E79.bottom"),sQuery(id+"F63.wireOp",EDGE,"E79.left")])]})]});
            var Q3;
            Q3=makeQuery(id+"F64.boolean.opBoolean","MERGE",EDGE,{"derivedFrom":[makeQuery(id+"F31.opExtrude","SWEPT_EDGE",EDGE,{"disambiguationData":[OSD([sQuery(id+"F30.wireOp",EDGE,"E29.bottom"),sQuery(id+"F30.wireOp",EDGE,"E29.right")])]}),makeQuery(id+"F64.opExtrude","SWEPT_EDGE",EDGE,{"disambiguationData":[OSD([sQuery(id+"F63.wireOp",EDGE,"E79.top"),sQuery(id+"F63.wireOp",EDGE,"E79.left")])]})]});
            var Q4;
            Q4=makeQuery(id+"F64.opExtrude","CAP_EDGE",EDGE,{"disambiguationData":[OSD([sQuery(id+"F63.wireOp",EDGE,"E79.right")])],"isStart":false});
            var Q5;
            Q5=makeQuery(id+"F55.opPattern","COPY",EDGE,{"derivedFrom":makeQuery(id+"F54.opExtrude","CAP_EDGE",EDGE,{"disambiguationData":[OSD([sQuery(id+"F53.wireOp",EDGE,"E62")])],"isStart":false}),"instanceName":"1"});
            var Q6;
            Q6=makeQuery(id+"F64.opExtrude","CAP_EDGE",EDGE,{"disambiguationData":[OSD([sQuery(id+"F63.wireOp",EDGE,"E79.left")])],"isStart":false});
            var Q7;
            Q7=makeQuery(id+"F55.opPattern","COPY",EDGE,{"derivedFrom":makeQuery(id+"F54.opExtrude","CAP_EDGE",EDGE,{"disambiguationData":[OSD([sQuery(id+"F53.wireOp",EDGE,"E62")])],"isStart":true}),"instanceName":"1"});
            var Q8;
            Q8=makeQuery(id+"F55.opPattern","COPY",EDGE,{"derivedFrom":makeQuery(id+"F54.opExtrude","SWEPT_EDGE",EDGE,{"disambiguationData":[OSD([sQuery(id+"F53.wireOp",EDGE,"E61"),sQuery(id+"F53.wireOp",EDGE,"E62")])]}),"instanceName":"1"});
            var Q9;
            Q9=makeQuery(id+"F54.opExtrude","SWEPT_EDGE",EDGE,{"disambiguationData":[OSD([sQuery(id+"F53.wireOp",EDGE,"E61"),sQuery(id+"F53.wireOp",EDGE,"E62")])]});
            var Q10;
            Q10=makeQuery(id+"F54.opExtrude","CAP_EDGE",EDGE,{"disambiguationData":[OSD([sQuery(id+"F53.wireOp",EDGE,"E62")])],"isStart":false});
            var Q11;
            Q11=makeQuery(id+"F54.opExtrude","CAP_EDGE",EDGE,{"disambiguationData":[OSD([sQuery(id+"F53.wireOp",EDGE,"E62")])],"isStart":true});
            var Q12;
            Q12=makeQuery(id+"F61.opExtrude","CAP_EDGE",EDGE,{"disambiguationData":[OSD([sQuery(id+"F60.wireOp",EDGE,"E75")])],"isStart":false});
            var Q13;
            Q13=makeQuery(id+"F61.opExtrude","CAP_EDGE",EDGE,{"disambiguationData":[OSD([sQuery(id+"F60.wireOp",EDGE,"E75")])],"isStart":true});
            var Q14;
            Q14=makeQuery(id+"F62.opPattern","COPY",EDGE,{"derivedFrom":makeQuery(id+"F61.opExtrude","CAP_EDGE",EDGE,{"disambiguationData":[OSD([sQuery(id+"F60.wireOp",EDGE,"E75")])],"isStart":true}),"instanceName":"1"});
            var Q15;
            Q15=makeQuery(id+"F62.opPattern","COPY",EDGE,{"derivedFrom":makeQuery(id+"F61.opExtrude","CAP_EDGE",EDGE,{"disambiguationData":[OSD([sQuery(id+"F60.wireOp",EDGE,"E75")])],"isStart":false}),"instanceName":"1"});
            var Q16;
            Q16=makeQuery(id+"F61.opExtrude","SWEPT_FACE",FACE,{"disambiguationData":[OSD([sQuery(id+"F60.wireOp",EDGE,"E75")])]});
            var Q17;
            Q17=makeQuery(id+"F62.opPattern","COPY",EDGE,{"derivedFrom":makeQuery(id+"F61.opExtrude","SWEPT_EDGE",EDGE,{"disambiguationData":[OSD([sQuery(id+"F60.wireOp",EDGE,"E74"),sQuery(id+"F60.wireOp",EDGE,"E75")])]}),"instanceName":"1"});
            var Q18;
            Q18=makeQuery(id+"F31.opExtrude","CAP_EDGE",EDGE,{"disambiguationData":[OSD([sQuery(id+"F30.wireOp",EDGE,"E29.top")])],"isStart":true});
            var Q19;
            Q19=makeQuery(id+"F31.opExtrude","CAP_EDGE",EDGE,{"disambiguationData":[OSD([sQuery(id+"F30.wireOp",EDGE,"E29.bottom")])],"isStart":true});
            var Q20;
            Q20=makeQuery(id+"F31.opExtrude","CAP_EDGE",EDGE,{"disambiguationData":[OSD([sQuery(id+"F30.wireOp",EDGE,"E29.left")])],"isStart":true});
            var Q21;
            Q21=makeQuery(id+"F31.opExtrude","CAP_EDGE",EDGE,{"disambiguationData":[OSD([sQuery(id+"F30.wireOp",EDGE,"E29.right")])],"isStart":true});
            fillet(context, id + "F65", {"entities" : qUnion([Q0, Q1, Q2, Q3, Q4, Q5, Q6, Q7, Q8, Q9, Q10, Q11, Q12, Q13, Q14, Q15, Q16, Q17, Q18, Q19, Q20, Q21]), "radius" : 1 * mm, "tangentPropagation" : true, "allowEdgeOverflow" : false});
        }
    });
